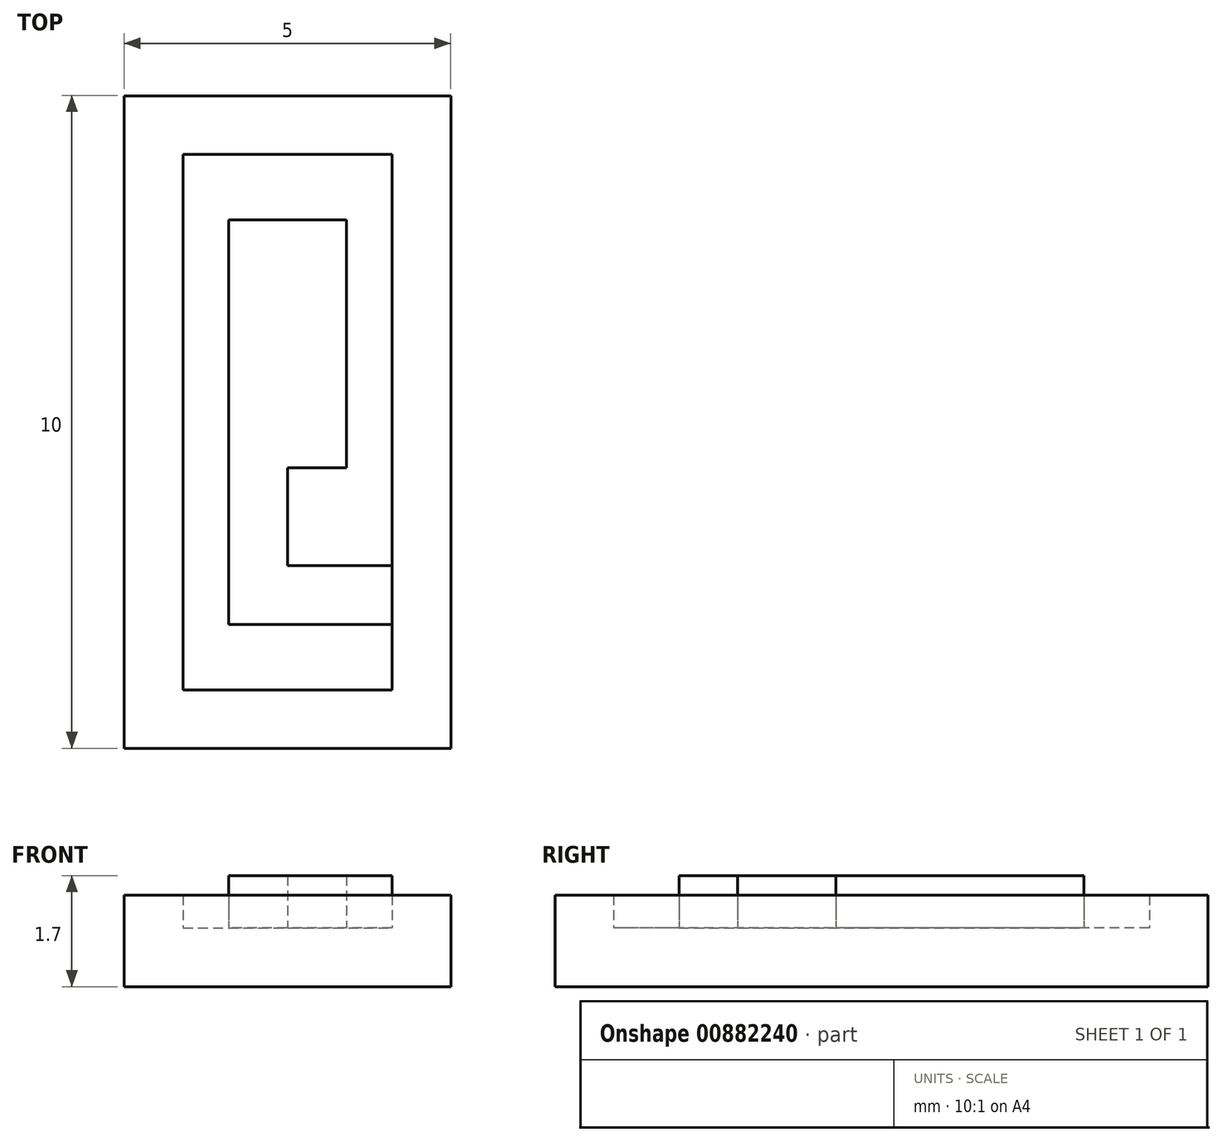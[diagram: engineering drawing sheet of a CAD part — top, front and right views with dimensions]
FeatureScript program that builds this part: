
annotation { "Feature Type Name" : "Feature", "Feature Type Description" : "" }
export const myFeature = defineFeature(function(context is Context, id is Id, definition is map)
    precondition{}
    {
        {
            var Q0;
            Q0=qCreatedBy(makeId("Top.planeOp"),FACE);
            var sketch = newSketch(context, id + "F0", { "sketchPlane" : qUnion([Q0])});
            skLineSegment(sketch, "E0.bottom", {"start": v(0.9, 7.83) * mm, "end": v(5.9, 7.83) * mm});
            skLineSegment(sketch, "E0.top", {"start": v(0.9, -2.17) * mm, "end": v(5.9, -2.17) * mm});
            skLineSegment(sketch, "E0.left", {"start": v(0.9, 7.83) * mm, "end": v(0.9, -2.17) * mm});
            skLineSegment(sketch, "E0.right", {"start": v(5.9, 7.83) * mm, "end": v(5.9, -2.17) * mm});
            skSolve(sketch);
        }
        {
            var Q0;
            Q0=makeQuery(id+"F0.imprint","IMPRINT",FACE,{"disambiguationData":[TD([[makeQuery(id+"F0.imprint","IMPRINT",EDGE,{"derivedFrom":sQuery(id+"F0.wireOp",EDGE,"E0.bottom")}),-1.0]])]});
            extrude(context, id + "F1", {"entities" : qUnion([Q0]), "depth" : 1.4 * mm, "offsetDistance" : 25 * mm});
        }
        {
            var Q0;
            Q0=makeQuery(id+"F1.opExtrude","CAP_FACE",FACE,{"disambiguationData":[OSD([sQuery(id+"F0.wireOp",EDGE,"E0.bottom"),sQuery(id+"F0.wireOp",EDGE,"E0.top"),sQuery(id+"F0.wireOp",EDGE,"E0.left"),sQuery(id+"F0.wireOp",EDGE,"E0.right")])],"isStart":false});
            shell(context, id + "F2", {"entities" : qUnion([Q0]), "thickness" : 0.9 * mm});
        }
        {
            var Q0;
            Q0=makeQuery(id+"F2.opShell","OFFSET_FACE",FACE,{"disambiguationData":[OSD([sQuery(id+"F0.wireOp",EDGE,"E0.bottom"),sQuery(id+"F0.wireOp",EDGE,"E0.top"),sQuery(id+"F0.wireOp",EDGE,"E0.left"),sQuery(id+"F0.wireOp",EDGE,"E0.right")])]});
            var sketch = newSketch(context, id + "F3", { "sketchPlane" : qUnion([Q0])});
            skLineSegment(sketch, "E1", {"start": v(5, 0.63) * mm, "end": v(3.4, 0.63) * mm});
            skLineSegment(sketch, "E2", {"start": v(3.4, 0.63) * mm, "end": v(3.4, 5.03) * mm});
            skLineSegment(sketch, "E3", {"start": v(3.4, 5.03) * mm, "end": v(3.4, 5.03) * mm});
            skLineSegment(sketch, "E4", {"start": v(3.4, 5.03) * mm, "end": v(3.4, 2.13) * mm});
            skLineSegment(sketch, "E5.0", {"start": v(4.3, 5.93) * mm, "end": v(4.3, 2.13) * mm});
            skLineSegment(sketch, "E5.1", {"start": v(2.5, 5.93) * mm, "end": v(4.3, 5.93) * mm});
            skLineSegment(sketch, "E5.2", {"start": v(2.5, -0.27) * mm, "end": v(2.5, 5.93) * mm});
            skLineSegment(sketch, "E5.3", {"start": v(5, -0.27) * mm, "end": v(2.5, -0.27) * mm});
            skLineSegment(sketch, "E6", {"start": v(3.4, 2.13) * mm, "end": v(4.3, 2.13) * mm});
            skSolve(sketch);
        }
        {
            var Q0;
            {var subQ0=sQuery(id+"F3.wireOp",EDGE,"E1");Q0=makeQuery(id+"F3.imprint","IMPRINT",FACE,{"disambiguationData":[TD([[makeQuery(id+"F3.imprint","IMPRINT",EDGE,{"derivedFrom":subQ0}),1.0]])]});}
            extrude(context, id + "F4", {"entities" : qUnion([Q0]), "operationType" : NewBodyOperationType.ADD, "depth" : 0.8 * mm, "offsetDistance" : 25 * mm});
        }
    });
